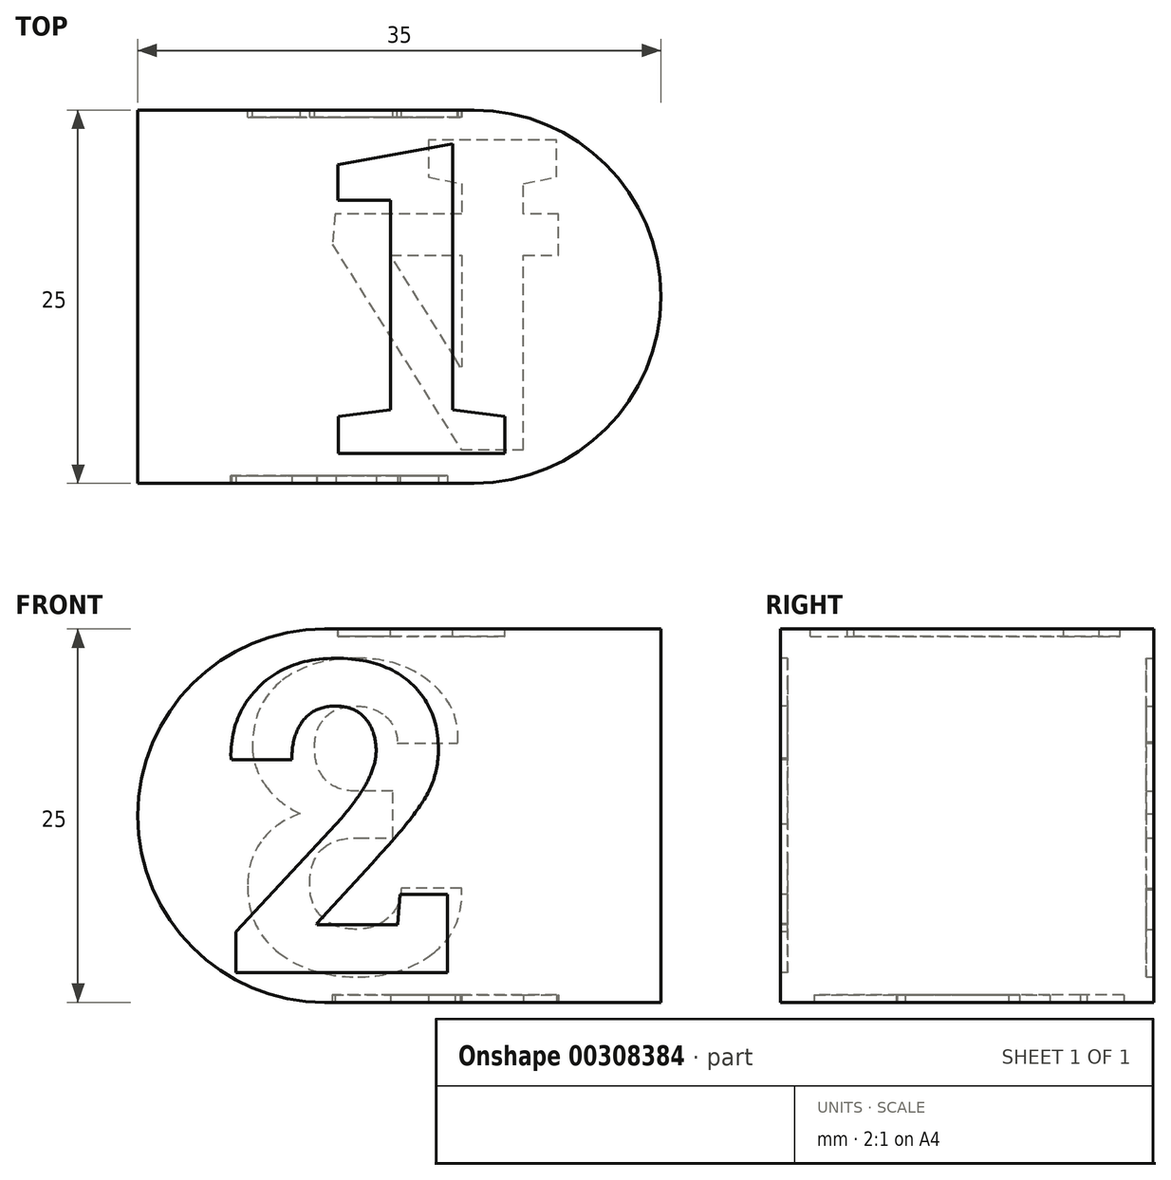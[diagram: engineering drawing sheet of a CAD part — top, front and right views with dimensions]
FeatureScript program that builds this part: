
annotation { "Feature Type Name" : "Feature", "Feature Type Description" : "" }
export const myFeature = defineFeature(function(context is Context, id is Id, definition is map)
    precondition{}
    {
        {
            var Q0;
            Q0=qCreatedBy(makeId("Top.planeOp"),FACE);
            var sketch = newSketch(context, id + "F0", { "sketchPlane" : qUnion([Q0])});
            skLineSegment(sketch, "E0.bottom", {"start": v(0, 0) * mm, "end": v(35, 0) * mm});
            skLineSegment(sketch, "E0.top", {"start": v(0, 25) * mm, "end": v(35, 25) * mm});
            skLineSegment(sketch, "E0.left", {"start": v(0, 0) * mm, "end": v(0, 25) * mm});
            skLineSegment(sketch, "E0.right", {"start": v(35, 0) * mm, "end": v(35, 25) * mm});
            skSolve(sketch);
        }
        {
            var Q0;
            Q0=makeQuery(id+"F0.imprint","IMPRINT",FACE,{"disambiguationData":[TD([[makeQuery(id+"F0.imprint","IMPRINT",EDGE,{"derivedFrom":sQuery(id+"F0.wireOp",EDGE,"E0.bottom")}),1.0]])]});
            extrude(context, id + "F1", {"entities" : qUnion([Q0]), "depth" : 25 * mm});
        }
        {
            var Q0;
            Q0=makeQuery(id+"F1.opExtrude","CAP_EDGE",EDGE,{"disambiguationData":[OSD([sQuery(id+"F0.wireOp",EDGE,"E0.left")])],"isStart":false});
            var Q1;
            Q1=makeQuery(id+"F1.opExtrude","CAP_EDGE",EDGE,{"disambiguationData":[OSD([sQuery(id+"F0.wireOp",EDGE,"E0.left")])],"isStart":true});
            fillet(context, id + "F2", {"entities" : qUnion([Q0, Q1]), "radius" : 12.5 * mm, "tangentPropagation" : true, "allowEdgeOverflow" : false});
        }
        {
            var Q0;
            Q0=makeQuery(id+"F1.opExtrude","SWEPT_EDGE",EDGE,{"disambiguationData":[OSD([sQuery(id+"F0.wireOp",EDGE,"E0.bottom"),sQuery(id+"F0.wireOp",EDGE,"E0.right")])]});
            var Q1;
            Q1=makeQuery(id+"F1.opExtrude","SWEPT_EDGE",EDGE,{"disambiguationData":[OSD([sQuery(id+"F0.wireOp",EDGE,"E0.top"),sQuery(id+"F0.wireOp",EDGE,"E0.right")])]});
            fillet(context, id + "F3", {"entities" : qUnion([Q0, Q1]), "radius" : 12.5 * mm, "tangentPropagation" : true, "allowEdgeOverflow" : false});
        }
        {
            var Q0;
            Q0=makeQuery(id+"F1.opExtrude","CAP_FACE",FACE,{"disambiguationData":[OSD([sQuery(id+"F0.wireOp",EDGE,"E0.bottom"),sQuery(id+"F0.wireOp",EDGE,"E0.top"),sQuery(id+"F0.wireOp",EDGE,"E0.left"),sQuery(id+"F0.wireOp",EDGE,"E0.right")])],"isStart":false});
            var sketch = newSketch(context, id + "F4", { "sketchPlane" : qUnion([Q0])});
            skText(sketch, "E1", { "text": "1", "fontName": "RobotoSlab-Bold.ttf"});
            skLineSegment(sketch, "E2", {"start": v(19.43, 23) * mm, "end": v(19.43, 25) * mm, "construction": true});
            skLineSegment(sketch, "E3", {"start": v(19.43, 2) * mm, "end": v(19.43, 0) * mm, "construction": true});
            const initialGuessF4  = {"E1": [0.0125, 0.002, 1, 0, 0.021]};
            skSetInitialGuess(sketch, initialGuessF4);
            skSolve(sketch);
        }
        {
            var Q0;
            Q0=makeQuery(id+"F1.opExtrude","CAP_FACE",FACE,{"disambiguationData":[OSD([sQuery(id+"F0.wireOp",EDGE,"E0.bottom"),sQuery(id+"F0.wireOp",EDGE,"E0.top"),sQuery(id+"F0.wireOp",EDGE,"E0.left"),sQuery(id+"F0.wireOp",EDGE,"E0.right")])],"isStart":true});
            var sketch = newSketch(context, id + "F5", { "sketchPlane" : qUnion([Q0])});
            skText(sketch, "E4", { "text": "4", "fontName": "RobotoSlab-Bold.ttf"});
            skLineSegment(sketch, "E5", {"start": v(21.23, -2) * mm, "end": v(21.23, 0) * mm, "construction": true});
            skLineSegment(sketch, "E6", {"start": v(21.23, -23) * mm, "end": v(21.23, -25) * mm, "construction": true});
            skPoint(sketch, "E6.endSnap0", {"position": v(17.5, -25) * mm});
            const initialGuessF5  = {"E4": [0.0125, -0.023, 1, 0, 0.021]};
            skSetInitialGuess(sketch, initialGuessF5);
            skSolve(sketch);
        }
        {
            var Q0;
            Q0=makeQuery(id+"F1.opExtrude","SWEPT_FACE",FACE,{"disambiguationData":[OSD([sQuery(id+"F0.wireOp",EDGE,"E0.bottom")])]});
            var sketch = newSketch(context, id + "F6", { "sketchPlane" : qUnion([Q0])});
            skText(sketch, "E7", { "text": "2", "fontName": "RobotoSlab-Bold.ttf"});
            skLineSegment(sketch, "E8", {"start": v(14, 23) * mm, "end": v(14, 25) * mm, "construction": true});
            skLineSegment(sketch, "E9", {"start": v(14, 2) * mm, "end": v(14, 0) * mm, "construction": true});
            const initialGuessF6  = {"E7": [0.00552, 0.002, 1, 0, 0.021]};
            skSetInitialGuess(sketch, initialGuessF6);
            skSolve(sketch);
        }
        {
            var Q0;
            Q0=makeQuery(id+"F1.opExtrude","SWEPT_FACE",FACE,{"disambiguationData":[OSD([sQuery(id+"F0.wireOp",EDGE,"E0.top")])]});
            var sketch = newSketch(context, id + "F7", { "sketchPlane" : qUnion([Q0])});
            skText(sketch, "E10", { "text": "3", "fontName": "RobotoSlab-Bold.ttf"});
            skLineSegment(sketch, "E11", {"start": v(-14.03, 2) * mm, "end": v(-14.03, 0) * mm, "construction": true});
            skLineSegment(sketch, "E12", {"start": v(-14.03, 23) * mm, "end": v(-14.03, 25) * mm, "construction": true});
            const initialGuessF7  = {"E10": [-0.0225, 0.002, 1, 0, 0.021]};
            skSetInitialGuess(sketch, initialGuessF7);
            skSolve(sketch);
        }
        {
            var Q0;
            Q0 = qSketchRegion(id + "F4", true);
            extrude(context, id + "F8", {"entities" : qUnion([Q0]), "operationType" : NewBodyOperationType.REMOVE, "oppositeDirection" : true, "depth" : .5 * mm});
        }
        {
            var Q0;
            Q0 = qSketchRegion(id + "F5", true);
            extrude(context, id + "F9", {"entities" : qUnion([Q0]), "operationType" : NewBodyOperationType.REMOVE, "oppositeDirection" : true, "depth" : .5 * mm});
        }
        {
            var Q0;
            Q0 = qSketchRegion(id + "F6", true);
            extrude(context, id + "F10", {"entities" : qUnion([Q0]), "operationType" : NewBodyOperationType.REMOVE, "oppositeDirection" : true, "depth" : .5 * mm});
        }
        {
            var Q0;
            Q0 = qSketchRegion(id + "F7", true);
            extrude(context, id + "F11", {"entities" : qUnion([Q0]), "operationType" : NewBodyOperationType.REMOVE, "oppositeDirection" : true, "depth" : .5 * mm});
        }
    });
